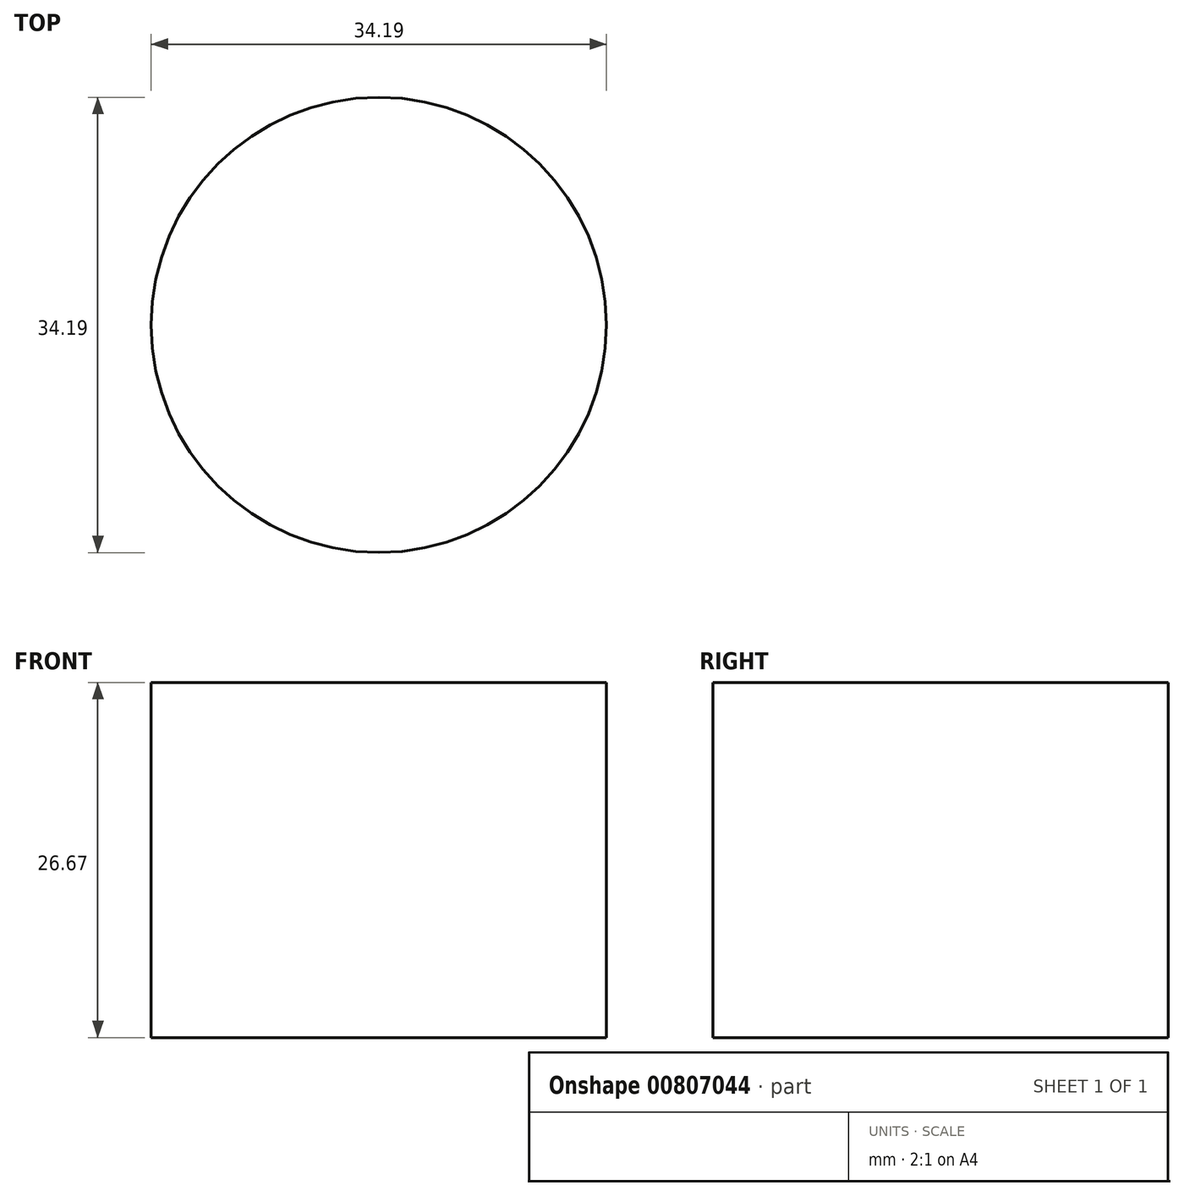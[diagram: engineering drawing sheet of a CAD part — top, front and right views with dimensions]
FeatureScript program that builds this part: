
annotation { "Feature Type Name" : "Feature", "Feature Type Description" : "" }
export const myFeature = defineFeature(function(context is Context, id is Id, definition is map)
    precondition{}
    {
        {
            var Q0;
            Q0=qCreatedBy(makeId("Top.planeOp"),FACE);
            var sketch = newSketch(context, id + "F0", { "sketchPlane" : qUnion([Q0])});
            skCircle(sketch, "E0", {"center": v(-0.22, 5.15) * mm, "radius": 17.1 * mm});
            skSolve(sketch);
        }
        {
            var Q0;
            Q0=sQuery(id+"F0.wireOp",EDGE,"E0");
            extrude(context, id + "F1", {"bodyType" : ToolBodyType.SURFACE, "surfaceEntities" : qUnion([Q0]), "depth" : 26.67 * mm, "offsetDistance" : 25.4 * mm});
        }
    });
